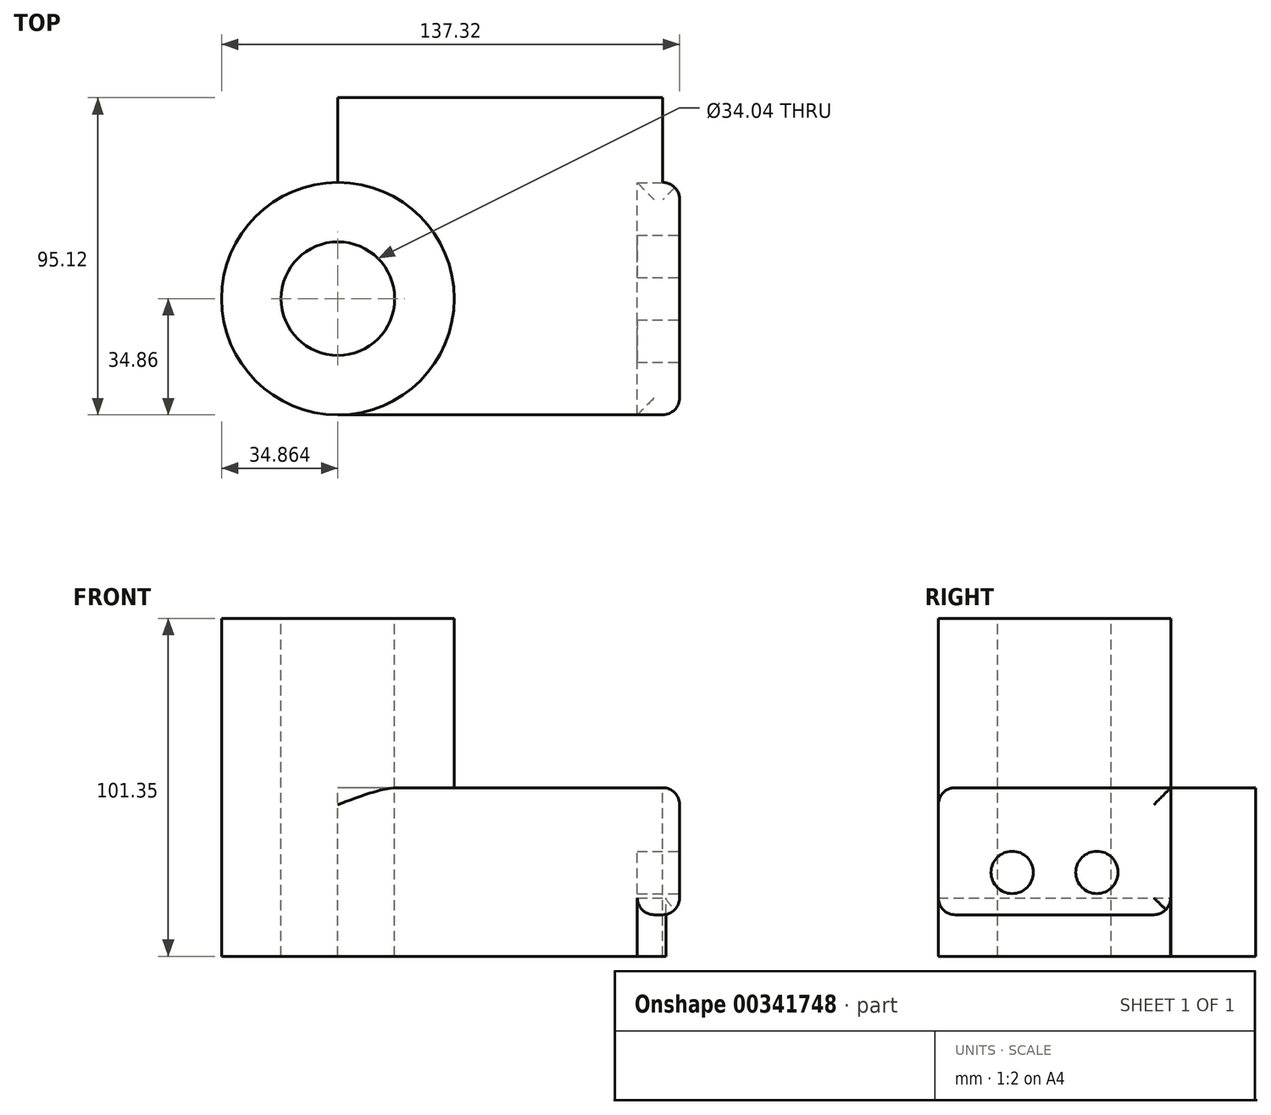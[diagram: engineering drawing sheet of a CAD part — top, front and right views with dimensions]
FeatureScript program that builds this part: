
annotation { "Feature Type Name" : "Feature", "Feature Type Description" : "" }
export const myFeature = defineFeature(function(context is Context, id is Id, definition is map)
    precondition{}
    {
        {
            var Q0;
            Q0=qCreatedBy(makeId("Top.planeOp"),FACE);
            var sketch = newSketch(context, id + "F0", { "sketchPlane" : qUnion([Q0])});
            skLineSegment(sketch, "E0.bottom", {"start": v(51.23, -34.86) * mm, "end": v(-51.23, -34.86) * mm});
            skLineSegment(sketch, "E0.top", {"start": v(51.23, 34.86) * mm, "end": v(-51.23, 34.86) * mm});
            skLineSegment(sketch, "E0.left", {"start": v(51.23, -34.86) * mm, "end": v(51.23, 34.86) * mm});
            skLineSegment(sketch, "E0.right", {"start": v(-51.23, -34.86) * mm, "end": v(-51.23, 34.86) * mm});
            skPoint(sketch, "E0.middle", {"position": v(0, 0) * mm});
            skCircle(sketch, "E1", {"center": v(-51.23, 0) * mm, "radius": 34.86 * mm});
            skCircle(sketch, "E2", {"center": v(-51.23, 0) * mm, "radius": 17.02 * mm});
            skSolve(sketch);
        }
        {
            var Q0;
            Q0 = qSketchRegion(id + "F0", true);
            extrude(context, id + "F1", {"entities" : qUnion([Q0]), "oppositeDirection" : true, "depth" : 12.7 * mm});
        }
        {
            var Q0;
            {var subQ1=sQuery(id+"F0.wireOp",EDGE,"E0.right");var subQ3=sQuery(id+"F0.wireOp",EDGE,"E2");var subQ4=makeQuery(id+"F0.imprint","INTERSECT",VERTEX,{"disambiguationData":[OD(0.0)],"derivedFrom":[subQ1,subQ3]});Q0=makeQuery(id+"F0.imprint","IMPRINT",FACE,{"disambiguationData":[TD([[makeQuery(id+"F0.imprint","IMPRINT",EDGE,{"disambiguationData":[TD([[subQ4,-1.0]])],"derivedFrom":subQ3}),-1.0]])]});}
            var Q1;
            {var subQ1=sQuery(id+"F0.wireOp",EDGE,"E0.right");var subQ3=sQuery(id+"F0.wireOp",EDGE,"E2");var subQ4=makeQuery(id+"F0.imprint","INTERSECT",VERTEX,{"disambiguationData":[OD(0.0)],"derivedFrom":[subQ1,subQ3]});Q1=makeQuery(id+"F0.imprint","IMPRINT",FACE,{"disambiguationData":[TD([[makeQuery(id+"F0.imprint","IMPRINT",EDGE,{"disambiguationData":[TD([[subQ4,1.0]])],"derivedFrom":subQ3}),-1.0]])]});}
            extrude(context, id + "F2", {"entities" : qUnion([Q0, Q1]), "operationType" : NewBodyOperationType.ADD, "depth" : 50.8 * mm});
        }
        {
            var Q0;
            Q0=makeQuery(id+"F1.opExtrude","SWEPT_FACE",FACE,{"disambiguationData":[OSD([sQuery(id+"F0.wireOp",EDGE,"E0.left")])]});
            var sketch = newSketch(context, id + "F3", { "sketchPlane" : qUnion([Q0])});
            skLineSegment(sketch, "E3.bottom", {"start": v(-34.86, 0) * mm, "end": v(34.77, 0) * mm});
            skLineSegment(sketch, "E3.top", {"start": v(-34.86, -38.1) * mm, "end": v(34.77, -38.1) * mm});
            skLineSegment(sketch, "E3.left", {"start": v(-34.86, 0) * mm, "end": v(-34.86, -38.1) * mm});
            skLineSegment(sketch, "E3.right", {"start": v(34.77, 0) * mm, "end": v(34.77, -38.1) * mm});
            skLineSegment(sketch, "E4.bottom", {"start": v(21.99, 64.63) * mm, "end": v(18.07, 64.63) * mm});
            skLineSegment(sketch, "E4.top", {"start": v(21.99, 71.94) * mm, "end": v(18.07, 71.94) * mm});
            skLineSegment(sketch, "E4.left", {"start": v(21.99, 64.63) * mm, "end": v(21.99, 71.94) * mm});
            skLineSegment(sketch, "E4.right", {"start": v(18.07, 64.63) * mm, "end": v(18.07, 71.94) * mm});
            skLineSegment(sketch, "E5.left", {"start": v(34.77, -38.1) * mm, "end": v(34.77, -38.1) * mm});
            skLineSegment(sketch, "E5.right", {"start": v(11.06, -38.1) * mm, "end": v(11.06, -38.1) * mm});
            skCircle(sketch, "E6", {"center": v(-12.7, -25.4) * mm, "radius": 6.35 * mm});
            skLineSegment(sketch, "E7", {"start": v(0, 0) * mm, "end": v(0, -38.1) * mm});
            skCircle(sketch, "E8.MirrorC", {"center": v(12.7, -25.4) * mm, "radius": 6.35 * mm});
            skSolve(sketch);
        }
        {
            var Q0;
            Q0 = qSketchRegion(id + "F3", true);
            extrude(context, id + "F4", {"entities" : qUnion([Q0]), "operationType" : NewBodyOperationType.ADD, "oppositeDirection" : true, "depth" : 12.7 * mm});
        }
        {
            var Q0;
            Q0=makeQuery(id+"F4.boolean.opBoolean","MERGE",EDGE,{"derivedFrom":[makeQuery(id+"F1.opExtrude","SWEPT_EDGE",EDGE,{"disambiguationData":[OSD([sQuery(id+"F0.wireOp",EDGE,"E0.bottom"),sQuery(id+"F0.wireOp",EDGE,"E0.left")])]}),makeQuery(id+"F4.opExtrude","CAP_EDGE",EDGE,{"disambiguationData":[OSD([sQuery(id+"F3.wireOp",EDGE,"E3.left")])],"isStart":true})]});
            fillet(context, id + "F5", {"entities" : qUnion([Q0]), "radius" : 5.08 * mm, "tangentPropagation" : true, "allowEdgeOverflow" : false});
        }
        {
            var Q0;
            Q0=makeQuery(id+"F1.opExtrude","SWEPT_EDGE",EDGE,{"disambiguationData":[OSD([sQuery(id+"F0.wireOp",EDGE,"E0.top"),sQuery(id+"F0.wireOp",EDGE,"E0.left")])]});
            var Q1;
            Q1=makeQuery(id+"F4.opExtrude","SWEPT_EDGE",EDGE,{"disambiguationData":[OSD([sQuery(id+"F3.wireOp",EDGE,"E3.top"),sQuery(id+"F3.wireOp",EDGE,"E3.right")])]});
            var Q2;
            Q2=makeQuery(id+"F4.opExtrude","SWEPT_EDGE",EDGE,{"disambiguationData":[OSD([sQuery(id+"F3.wireOp",EDGE,"E3.top"),sQuery(id+"F3.wireOp",EDGE,"E3.left")])]});
            var Q3;
            Q3=makeQuery(id+"F4.opExtrude","SWEPT_FACE",FACE,{"disambiguationData":[OSD([sQuery(id+"F3.wireOp",EDGE,"E3.top")])]});
            var Q4;
            Q4=makeQuery(id+"F1.opExtrude","CAP_EDGE",EDGE,{"disambiguationData":[OSD([sQuery(id+"F0.wireOp",EDGE,"E0.left")])],"isStart":true});
            var Q5;
            Q5=makeQuery(id+"F2.opExtrude","CAP_EDGE",EDGE,{"disambiguationData":[OSD([sQuery(id+"F0.wireOp",EDGE,"E1")])],"isStart":true});
            fillet(context, id + "F6", {"entities" : qUnion([Q0, Q1, Q2, Q3, Q4, Q5]), "radius" : 5.08 * mm, "tangentPropagation" : true, "allowEdgeOverflow" : false});
        }
        {
            var Q0;
            Q0=makeQuery(id+"F4.opExtrude","SWEPT_BODY",BODY,{"disambiguationData":[OSD([sQuery(id+"F3.wireOp",EDGE,"E4.bottom"),sQuery(id+"F3.wireOp",EDGE,"E4.top"),sQuery(id+"F3.wireOp",EDGE,"E4.left"),sQuery(id+"F3.wireOp",EDGE,"E4.right")])]});
            deleteBodies(context, id + "F7", {"entities" : qUnion([Q0])});
        }
        {
            var Q0;
            Q0=makeQuery(id+"F1.opExtrude","SWEPT_FACE",FACE,{"disambiguationData":[OSD([sQuery(id+"F0.wireOp",EDGE,"E0.top")])]});
            extrude(context, id + "F8", {"entities" : qUnion([Q0]), "operationType" : NewBodyOperationType.ADD, "depth" : 25.4 * mm});
        }
        {
            var Q0;
            Q0=sQuery(id+"F0.wireOp",EDGE,"E1");
            extrude(context, id + "F9", {"bodyType" : ToolBodyType.SURFACE, "surfaceEntities" : qUnion([Q0]), "oppositeDirection" : true, "depth" : 50.8 * mm});
        }
        {
            var Q0;
            {var subQ0=sQuery(id+"F0.wireOp",EDGE,"E0.top");Q0=makeQuery(id+"F8.boolean.opBoolean","MERGE",FACE,{"derivedFrom":[makeQuery(id+"F1.opExtrude","CAP_FACE",FACE,{"disambiguationData":[OSD([sQuery(id+"F0.wireOp",EDGE,"E0.bottom"),subQ0,sQuery(id+"F0.wireOp",EDGE,"E0.left"),sQuery(id+"F0.wireOp",EDGE,"E0.right"),sQuery(id+"F0.wireOp",EDGE,"E1"),sQuery(id+"F0.wireOp",EDGE,"E2"),sQuery(id+"F0.wireOp",EDGE,"ZQ92LLmq-AKHt-xKaN-ho3K-OnvJntIN2Mtw")])],"isStart":false}),makeQuery(id+"F8.opExtrude","SWEPT_FACE",FACE,{"disambiguationData":[OSD([subQ0]),TDD([makeQuery(id+"F1.opExtrude","CAP_EDGE",EDGE,{"disambiguationData":[OSD([subQ0])],"isStart":false})])]})]});}
            extrude(context, id + "F10", {"entities" : qUnion([Q0]), "operationType" : NewBodyOperationType.ADD, "depth" : 37.85 * mm});
        }
    });
